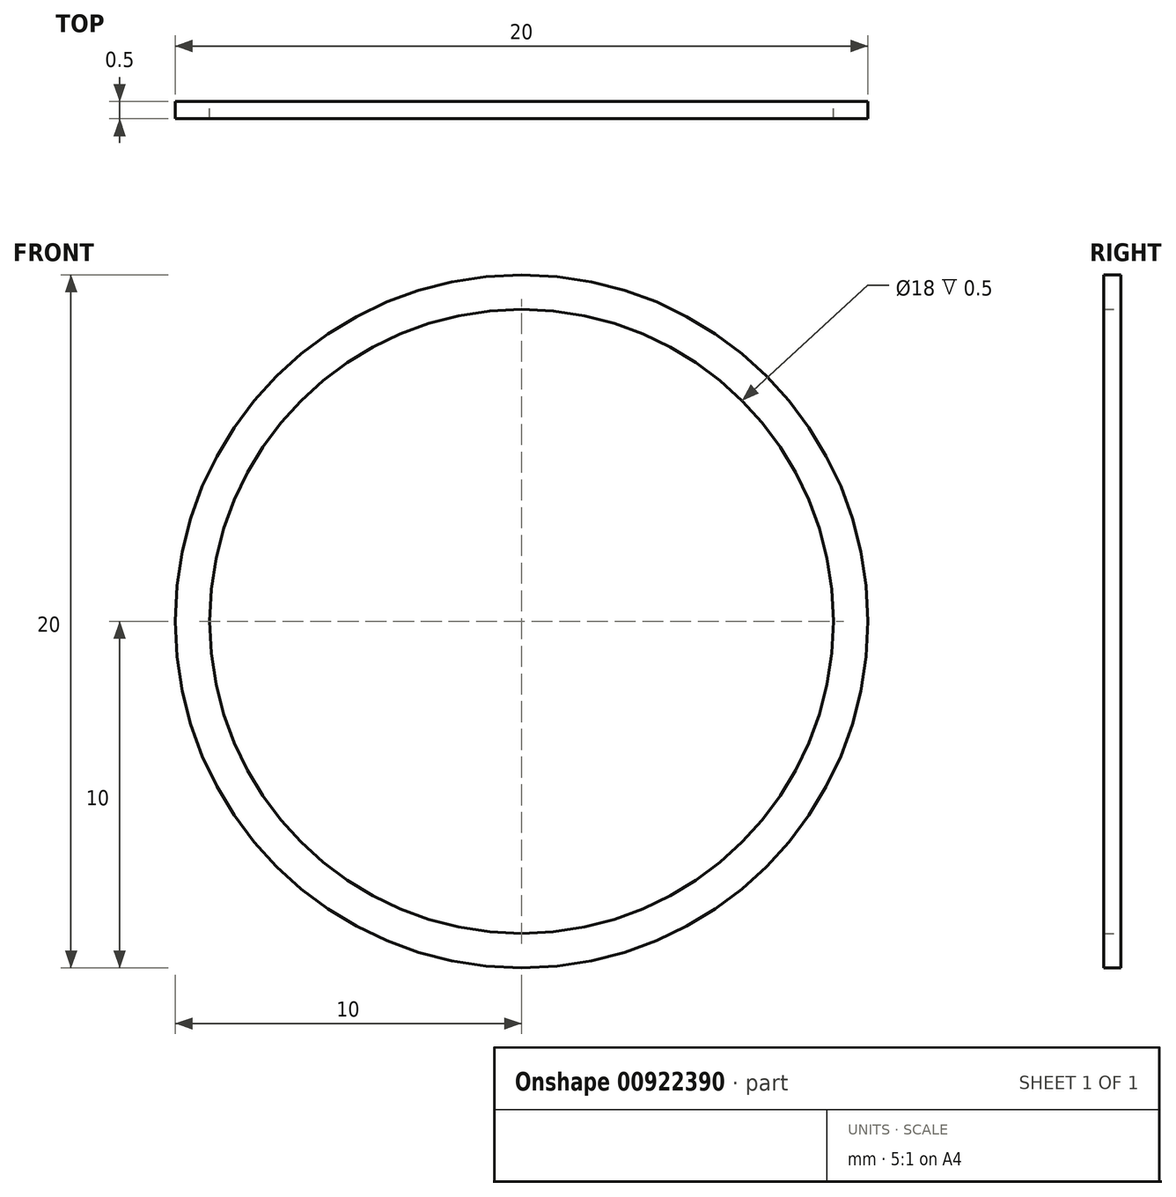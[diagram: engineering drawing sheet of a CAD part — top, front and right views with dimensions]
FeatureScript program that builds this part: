
annotation { "Feature Type Name" : "Feature", "Feature Type Description" : "" }
export const myFeature = defineFeature(function(context is Context, id is Id, definition is map)
    precondition{}
    {
        {
            var Q0;
            Q0=qCreatedBy(makeId("Front.planeOp"),FACE);
            var sketch = newSketch(context, id + "F0", { "sketchPlane" : qUnion([Q0])});
            skCircle(sketch, "E0", {"center": v(0, 0) * mm, "radius": 10 * mm});
            skCircle(sketch, "E1", {"center": v(0, 0) * mm, "radius": 9 * mm});
            skSolve(sketch);
        }
        {
            var Q0;
            Q0=makeQuery(id+"F0.imprint","IMPRINT",FACE,{"disambiguationData":[TD([[makeQuery(id+"F0.imprint","IMPRINT",EDGE,{"derivedFrom":sQuery(id+"F0.wireOp",EDGE,"E0")}),1.0]])]});
            extrude(context, id + "F1", {"entities" : qUnion([Q0]), "depth" : 0.5 * mm, "offsetDistance" : 25 * mm});
        }
    });
